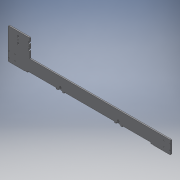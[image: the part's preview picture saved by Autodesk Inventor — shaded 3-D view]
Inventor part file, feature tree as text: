
AUTODESK INVENTOR PART (.ipt)
format: ipt  version: 2019 (Build 230136000, 136)  size: 373,248 bytes
history: native  units: in
note: dims shown in document units (in); Inventor stores cm internally (conversion verified against a paired STEP export)
features: reference x20, other x10, extrude x8, sketch x8, fillet x6, helix x2, projected_geometry x1
ambient origin geometry x8: Origin, YZ Plane, XZ Plane, XY Plane, X Axis, Y Axis, Z Axis, Center Point
bodies: Solid1 (feature_tree)
feature tree (55):
  extrude  "Extrusion1"  Depth=0.1181in
  fillet  "Fillet1"  Radius=0.1181in
  extrude  "Extrusion2"  Depth=0.1181in
  fillet  "Fillet2"  Radius=0.1181in
  fillet  "Fillet3"  Radius=0.1181in
  extrude  "Extrusion3"  Depth=0.1575in TaperAngle=0.0deg
  extrude  "Extrusion5"  Depth=0.0787in TaperAngle=0.0deg
  fillet  "Fillet5"  Radius=0.0787in
  extrude  "Extrusion6"  Depth=0.0787in
  extrude  "Extrusion7"  Depth=0.0079in
  extrude  "Extrusion8"  Depth=0.126in
  fillet  "Fillet6"  Radius=0.126in
  extrude  "Extrusion9"  Depth=0.1772in
  fillet  "Fillet7"  Radius=16.9291in
  sketch  "Sketch1"  dims[d0=0.1181in d1=0.1181in d2=0.1181in]
  reference  "Reference1"
  reference  "Reference2"
  reference  "Reference3"
  reference  "Reference4"
  reference  "Reference5"
  reference  "Reference6"
  sketch  "Sketch2"  dims[d3=0.1181in d4=0.1181in d5=0.1181in d6=0.1181in]
  projected_geometry  "Projected Loop1"
  sketch  "Sketch3"  dims[d7=0.1181in d8=0.1575in d9=0.0in]
  reference  "Reference7"
  reference  "Reference8"
  reference  "Reference9"
  reference  "Reference10"
  reference  "Reference11"
  reference  "Reference12"
  sketch  "Sketch6"  dims[d10=0.0787in d11=1.0in d12=0.0in d13=0.0787in]
  sketch  "Sketch7"  dims[d14=0.0787in d15=0.0079in]
  reference  "Reference16"
  reference  "Reference17"
  sketch  "Sketch8"  dims[d16=0.0079in d17=0.0079in]
  reference  "Reference18"
  reference  "Reference19"
  sketch  "Sketch9"  dims[d18=0.0079in d19=0.126in d20=0.126in]
  reference  "Reference20"
  reference  "Reference21"
  sketch  "Sketch10"  dims[d21=1.0in d22=0.0in d29=0.1772in d30=16.9291in d31=1.0in d32=0.0in d33=0.0394in d34=1.0in d35=0.0in d36=1.0in d37=0.0in d38=0.0079in d39=1.0in d40=0.0in d41=0.0394in d42=0.1181in d43=0.1181in d44=1.0in d45=0.0in d46=0.0394in d47=0.1575in d48=0.1575in]
  reference  "Reference22"
  reference  "Reference23"
  other  "<userpath>\Documents\CAD Files\Helix DLP\Helix DLP.iam"
  helix  "Helix DLP.iam"  [1 undecoded]
  other  "MGN12H, LINEAR GUIDE BLOCK:2"
  other  "MGN12H, LINEAR GUIDE BLOCK:1"
  other  "motor_brace_3:4"
  other  "motor_brace_3:3"
  other  "motor_brace_3:5"
  other  "motor_brace_3:6"
  other  "wiper 2:1"
  helix  "Helix DLP Z Stage:1"  [1 undecoded]
  other  "Z stage_side:2"
  other  "Z stage_side:1"
note: 2 required parameter values undecoded (feature->parameter linkage not recoverable at this tier; creation-order binding heuristic only, values carry confidence <= 0.55)
